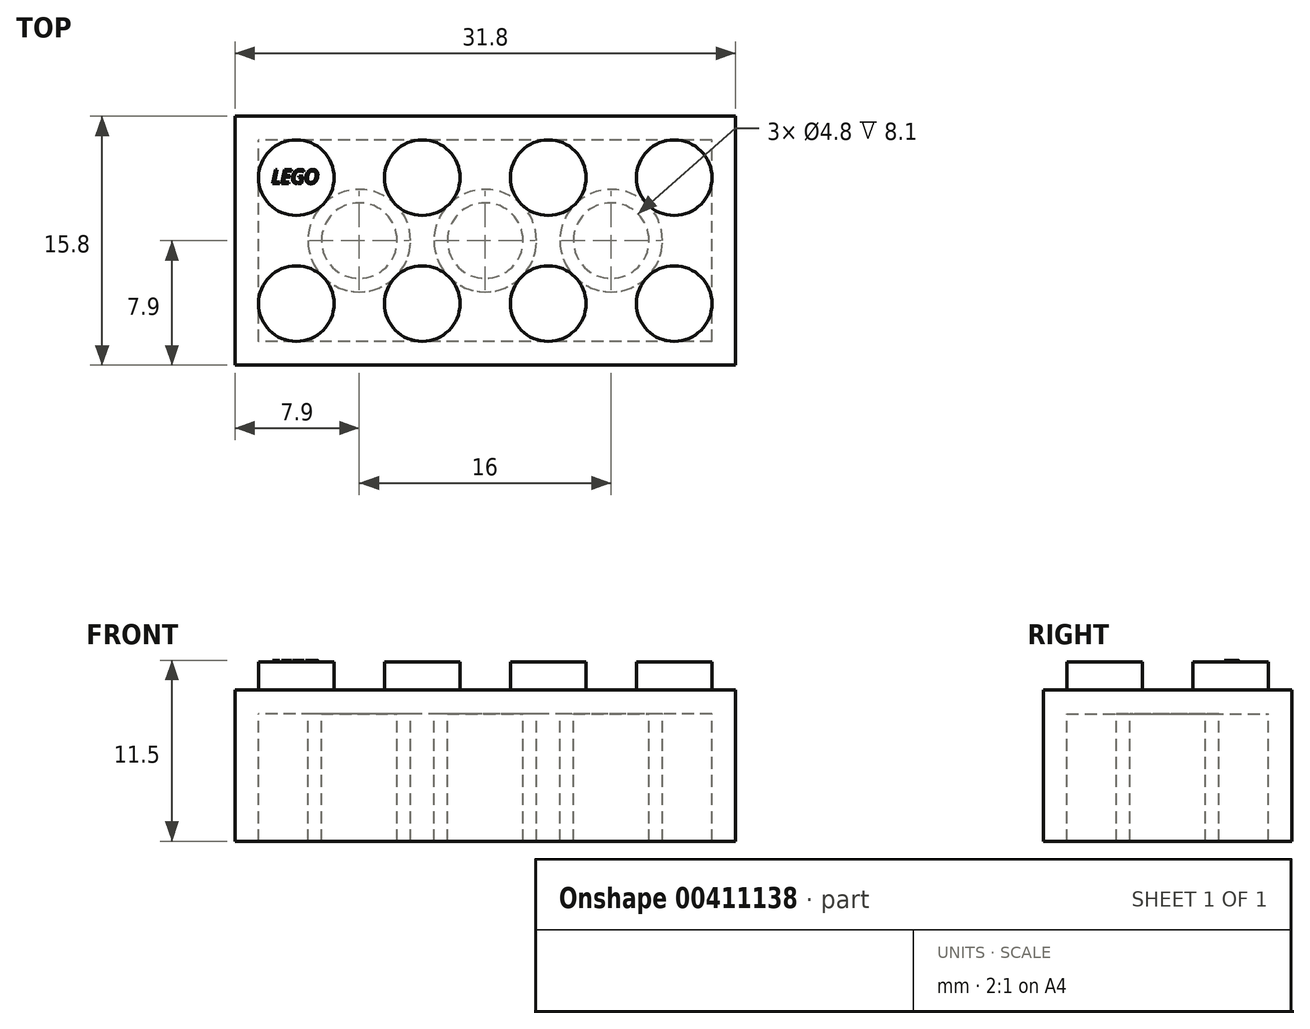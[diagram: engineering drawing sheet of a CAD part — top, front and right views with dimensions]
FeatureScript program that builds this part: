
annotation { "Feature Type Name" : "Feature", "Feature Type Description" : "" }
export const myFeature = defineFeature(function(context is Context, id is Id, definition is map)
    precondition{}
    {
        {
            assignVariable(context, id + "F0", {"name" : "base", "anyValue" : 0.8});
        }
        {
            assignVariable(context, id + "F1", {"name" : "knob_height", "anyValue" : 1.8});
        }
        {
            assignVariable(context, id + "F2", {"name" : "vertical_pitch", "anyValue" : getVariable(context, 'base') * 12});
        }
        {
            assignVariable(context, id + "F3", {"name" : "wall_thickness", "anyValue" : 1.5});
        }
        {
            var Q0;
            Q0=qCreatedBy(makeId("Top.planeOp"),FACE);
            var sketch = newSketch(context, id + "F4", { "sketchPlane" : qUnion([Q0])});
            skLineSegment(sketch, "E0.bottom", {"start": v(15.9, -7.9) * mm, "end": v(-15.9, -7.9) * mm});
            skLineSegment(sketch, "E0.top", {"start": v(15.9, 7.9) * mm, "end": v(-15.9, 7.9) * mm});
            skLineSegment(sketch, "E0.left", {"start": v(15.9, -7.9) * mm, "end": v(15.9, 7.9) * mm});
            skLineSegment(sketch, "E0.right", {"start": v(-15.9, -7.9) * mm, "end": v(-15.9, 7.9) * mm});
            skCircle(sketch, "E1", {"center": v(-12, 4) * mm, "radius": 2.4 * mm});
            skCircle(sketch, "E2.1.0.0", {"center": v(-12, -4) * mm, "radius": 2.4 * mm});
            skLineSegment(sketch, "E2.direction1", {"start": v(-12, 4) * mm, "end": v(-12, -4) * mm, "construction": true});
            skCircle(sketch, "E3.1.0.0", {"center": v(-4, 4) * mm, "radius": 2.4 * mm});
            skCircle(sketch, "E3.1.0.1", {"center": v(-4, -4) * mm, "radius": 2.4 * mm});
            skCircle(sketch, "E3.2.0.0", {"center": v(4, 4) * mm, "radius": 2.4 * mm});
            skCircle(sketch, "E3.2.0.1", {"center": v(4, -4) * mm, "radius": 2.4 * mm});
            skCircle(sketch, "E3.3.0.0", {"center": v(12, 4) * mm, "radius": 2.4 * mm});
            skCircle(sketch, "E3.3.0.1", {"center": v(12, -4) * mm, "radius": 2.4 * mm});
            skLineSegment(sketch, "E3.direction1", {"start": v(-12, 4) * mm, "end": v(-4, 4) * mm, "construction": true});
            skLineSegment(sketch, "E4", {"start": v(0, 9.3) * mm, "end": v(0, -10.01) * mm, "construction": true});
            skPoint(sketch, "E4.startSnap0", {"position": v(0, 7.9) * mm});
            skLineSegment(sketch, "E5", {"start": v(17.43, 0) * mm, "end": v(-18.24, 0) * mm, "construction": true});
            skPoint(sketch, "E5.startSnap0", {"position": v(15.9, 0) * mm});
            skLineSegment(sketch, "E6", {"start": v(-12, 7.9) * mm, "end": v(-12, 4) * mm, "construction": true});
            skLineSegment(sketch, "E7", {"start": v(-12, -4) * mm, "end": v(-12, -7.9) * mm, "construction": true});
            skLineSegment(sketch, "E8", {"start": v(15.9, 4) * mm, "end": v(12, 4) * mm, "construction": true});
            skLineSegment(sketch, "E9", {"start": v(-12, 4) * mm, "end": v(-15.9, 4) * mm, "construction": true});
            skSolve(sketch);
        }
        {
            var Q0;
            Q0=makeQuery(id+"F4.imprint","IMPRINT",FACE,{"disambiguationData":[TD([[makeQuery(id+"F4.imprint","IMPRINT",EDGE,{"derivedFrom":sQuery(id+"F4.wireOp",EDGE,"E0.bottom")}),-1.0]])]});
            var Q1;
            Q1=makeQuery(id+"F4.imprint","IMPRINT",FACE,{"disambiguationData":[TD([[makeQuery(id+"F4.imprint","IMPRINT",EDGE,{"derivedFrom":sQuery(id+"F4.wireOp",EDGE,"E1")}),1.0]])]});
            var Q2;
            Q2=makeQuery(id+"F4.imprint","IMPRINT",FACE,{"disambiguationData":[TD([[makeQuery(id+"F4.imprint","IMPRINT",EDGE,{"derivedFrom":sQuery(id+"F4.wireOp",EDGE,"E3.1.0.0")}),1.0]])]});
            var Q3;
            Q3=makeQuery(id+"F4.imprint","IMPRINT",FACE,{"disambiguationData":[TD([[makeQuery(id+"F4.imprint","IMPRINT",EDGE,{"derivedFrom":sQuery(id+"F4.wireOp",EDGE,"E3.2.0.0")}),1.0]])]});
            var Q4;
            Q4=makeQuery(id+"F4.imprint","IMPRINT",FACE,{"disambiguationData":[TD([[makeQuery(id+"F4.imprint","IMPRINT",EDGE,{"derivedFrom":sQuery(id+"F4.wireOp",EDGE,"E3.3.0.0")}),1.0]])]});
            var Q5;
            Q5=makeQuery(id+"F4.imprint","IMPRINT",FACE,{"disambiguationData":[TD([[makeQuery(id+"F4.imprint","IMPRINT",EDGE,{"derivedFrom":sQuery(id+"F4.wireOp",EDGE,"E3.3.0.1")}),1.0]])]});
            var Q6;
            Q6=makeQuery(id+"F4.imprint","IMPRINT",FACE,{"disambiguationData":[TD([[makeQuery(id+"F4.imprint","IMPRINT",EDGE,{"derivedFrom":sQuery(id+"F4.wireOp",EDGE,"E3.2.0.1")}),1.0]])]});
            var Q7;
            Q7=makeQuery(id+"F4.imprint","IMPRINT",FACE,{"disambiguationData":[TD([[makeQuery(id+"F4.imprint","IMPRINT",EDGE,{"derivedFrom":sQuery(id+"F4.wireOp",EDGE,"E3.1.0.1")}),1.0]])]});
            var Q8;
            Q8=makeQuery(id+"F4.imprint","IMPRINT",FACE,{"disambiguationData":[TD([[makeQuery(id+"F4.imprint","IMPRINT",EDGE,{"derivedFrom":sQuery(id+"F4.wireOp",EDGE,"E2.1.0.0")}),1.0]])]});
            extrude(context, id + "F5", {"entities" : qUnion([Q0, Q1, Q2, Q3, Q4, Q5, Q6, Q7, Q8]), "oppositeDirection" : true, "depth" : (getVariable(context, 'vertical_pitch')) * mm});
        }
        {
            var Q0;
            Q0=makeQuery(id+"F5.opExtrude","CAP_FACE",FACE,{"disambiguationData":[OSD([sQuery(id+"F4.wireOp",EDGE,"E0.bottom"),sQuery(id+"F4.wireOp",EDGE,"E0.top"),sQuery(id+"F4.wireOp",EDGE,"E0.left"),sQuery(id+"F4.wireOp",EDGE,"E0.right")])],"isStart":false});
            shell(context, id + "F6", {"entities" : qUnion([Q0]), "thickness" : 1.5 * mm});
        }
        {
            var Q0;
            Q0=makeQuery(id+"F4.imprint","IMPRINT",FACE,{"disambiguationData":[TD([[makeQuery(id+"F4.imprint","IMPRINT",EDGE,{"derivedFrom":sQuery(id+"F4.wireOp",EDGE,"E2.1.0.0")}),1.0]])]});
            var Q1;
            Q1=makeQuery(id+"F4.imprint","IMPRINT",FACE,{"disambiguationData":[TD([[makeQuery(id+"F4.imprint","IMPRINT",EDGE,{"derivedFrom":sQuery(id+"F4.wireOp",EDGE,"E1")}),1.0]])]});
            var Q2;
            Q2=makeQuery(id+"F4.imprint","IMPRINT",FACE,{"disambiguationData":[TD([[makeQuery(id+"F4.imprint","IMPRINT",EDGE,{"derivedFrom":sQuery(id+"F4.wireOp",EDGE,"E3.1.0.0")}),1.0]])]});
            var Q3;
            Q3=makeQuery(id+"F4.imprint","IMPRINT",FACE,{"disambiguationData":[TD([[makeQuery(id+"F4.imprint","IMPRINT",EDGE,{"derivedFrom":sQuery(id+"F4.wireOp",EDGE,"E3.2.0.0")}),1.0]])]});
            var Q4;
            Q4=makeQuery(id+"F4.imprint","IMPRINT",FACE,{"disambiguationData":[TD([[makeQuery(id+"F4.imprint","IMPRINT",EDGE,{"derivedFrom":sQuery(id+"F4.wireOp",EDGE,"E3.3.0.0")}),1.0]])]});
            var Q5;
            Q5=makeQuery(id+"F4.imprint","IMPRINT",FACE,{"disambiguationData":[TD([[makeQuery(id+"F4.imprint","IMPRINT",EDGE,{"derivedFrom":sQuery(id+"F4.wireOp",EDGE,"E3.3.0.1")}),1.0]])]});
            var Q6;
            Q6=makeQuery(id+"F4.imprint","IMPRINT",FACE,{"disambiguationData":[TD([[makeQuery(id+"F4.imprint","IMPRINT",EDGE,{"derivedFrom":sQuery(id+"F4.wireOp",EDGE,"E3.2.0.1")}),1.0]])]});
            var Q7;
            Q7=makeQuery(id+"F4.imprint","IMPRINT",FACE,{"disambiguationData":[TD([[makeQuery(id+"F4.imprint","IMPRINT",EDGE,{"derivedFrom":sQuery(id+"F4.wireOp",EDGE,"E3.1.0.1")}),1.0]])]});
            extrude(context, id + "F7", {"entities" : qUnion([Q0, Q1, Q2, Q3, Q4, Q5, Q6, Q7]), "operationType" : NewBodyOperationType.ADD, "depth" : (getVariable(context, 'knob_height')) * mm});
        }
        {
            var Q0;
            Q0=makeQuery(id+"F6.opShell","OFFSET_FACE",FACE,{"disambiguationData":[OSD([sQuery(id+"F4.wireOp",EDGE,"E0.bottom"),sQuery(id+"F4.wireOp",EDGE,"E0.top"),sQuery(id+"F4.wireOp",EDGE,"E0.left"),sQuery(id+"F4.wireOp",EDGE,"E0.right")])]});
            var sketch = newSketch(context, id + "F8", { "sketchPlane" : qUnion([Q0])});
            skCircle(sketch, "E10", {"center": v(-8, 0) * mm, "radius": 2.4 * mm});
            skCircle(sketch, "E11", {"center": v(-8, 0) * mm, "radius": 3.25 * mm});
            skCircle(sketch, "E12.1.0.0", {"center": v(0, 0) * mm, "radius": 2.4 * mm});
            skCircle(sketch, "E12.1.0.1", {"center": v(0, 0) * mm, "radius": 3.25 * mm});
            skCircle(sketch, "E12.2.0.0", {"center": v(8, 0) * mm, "radius": 2.4 * mm});
            skCircle(sketch, "E12.2.0.1", {"center": v(8, 0) * mm, "radius": 3.25 * mm});
            skLineSegment(sketch, "E12.direction1", {"start": v(-8, 0) * mm, "end": v(0, 0) * mm, "construction": true});
            skSolve(sketch);
        }
        {
            var Q0;
            Q0=makeQuery(id+"F8.imprint","IMPRINT",FACE,{"disambiguationData":[TD([[makeQuery(id+"F8.imprint","IMPRINT",EDGE,{"derivedFrom":sQuery(id+"F8.wireOp",EDGE,"E10")}),-1.0]])]});
            var Q1;
            Q1=makeQuery(id+"F8.imprint","IMPRINT",FACE,{"disambiguationData":[TD([[makeQuery(id+"F8.imprint","IMPRINT",EDGE,{"derivedFrom":sQuery(id+"F8.wireOp",EDGE,"E12.1.0.0")}),-1.0]])]});
            var Q2;
            Q2=makeQuery(id+"F8.imprint","IMPRINT",FACE,{"disambiguationData":[TD([[makeQuery(id+"F8.imprint","IMPRINT",EDGE,{"derivedFrom":sQuery(id+"F8.wireOp",EDGE,"E12.2.0.0")}),-1.0]])]});
            extrude(context, id + "F9", {"entities" : qUnion([Q0, Q1, Q2]), "operationType" : NewBodyOperationType.ADD, "depth" : (getVariable(context, 'vertical_pitch') - getVariable(context, 'wall_thickness')) * mm});
        }
        {
            var Q0;
            Q0=makeQuery(id+"F7.opExtrude","CAP_FACE",FACE,{"disambiguationData":[OSD([sQuery(id+"F4.wireOp",EDGE,"E1")])],"isStart":false});
            var sketch = newSketch(context, id + "F10", { "sketchPlane" : qUnion([Q0])});
            skText(sketch, "E13", { "text": "LEGO", "fontName": "OpenSans-Italic.ttf"});
            const initialGuessF10  = {"E13": [-0.01357, 0.00362, 1, 0, 0.0009]};
            skSetInitialGuess(sketch, initialGuessF10);
            skSolve(sketch);
        }
        {
            var Q0;
            Q0 = qSketchRegion(id + "F10", true);
            extrude(context, id + "F11", {"entities" : qUnion([Q0]), "operationType" : NewBodyOperationType.ADD, "depth" : 0.1 * mm});
        }
    });
